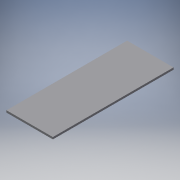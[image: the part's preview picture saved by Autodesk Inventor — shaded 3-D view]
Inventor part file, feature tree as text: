
AUTODESK INVENTOR PART (.ipt)
format: ipt  version: 2018.2 (Build 222227000, 227)  size: 90,112 bytes
history: native  units: in
note: dims shown in document units (in); Inventor stores cm internally (conversion verified against a paired STEP export)
features: extrude x1, sketch x1
ambient origin geometry x8: Origin, YZ Plane, XZ Plane, XY Plane, X Axis, Y Axis, Z Axis, Center Point
bodies: Solid1 (feature_tree)
feature tree (2):
  extrude  "Extrusion1"  Depth=45.381in
  sketch  "Sketch1"  dims[d0=17.459in d1=45.381in d2=0.75in d3=0.0in]
